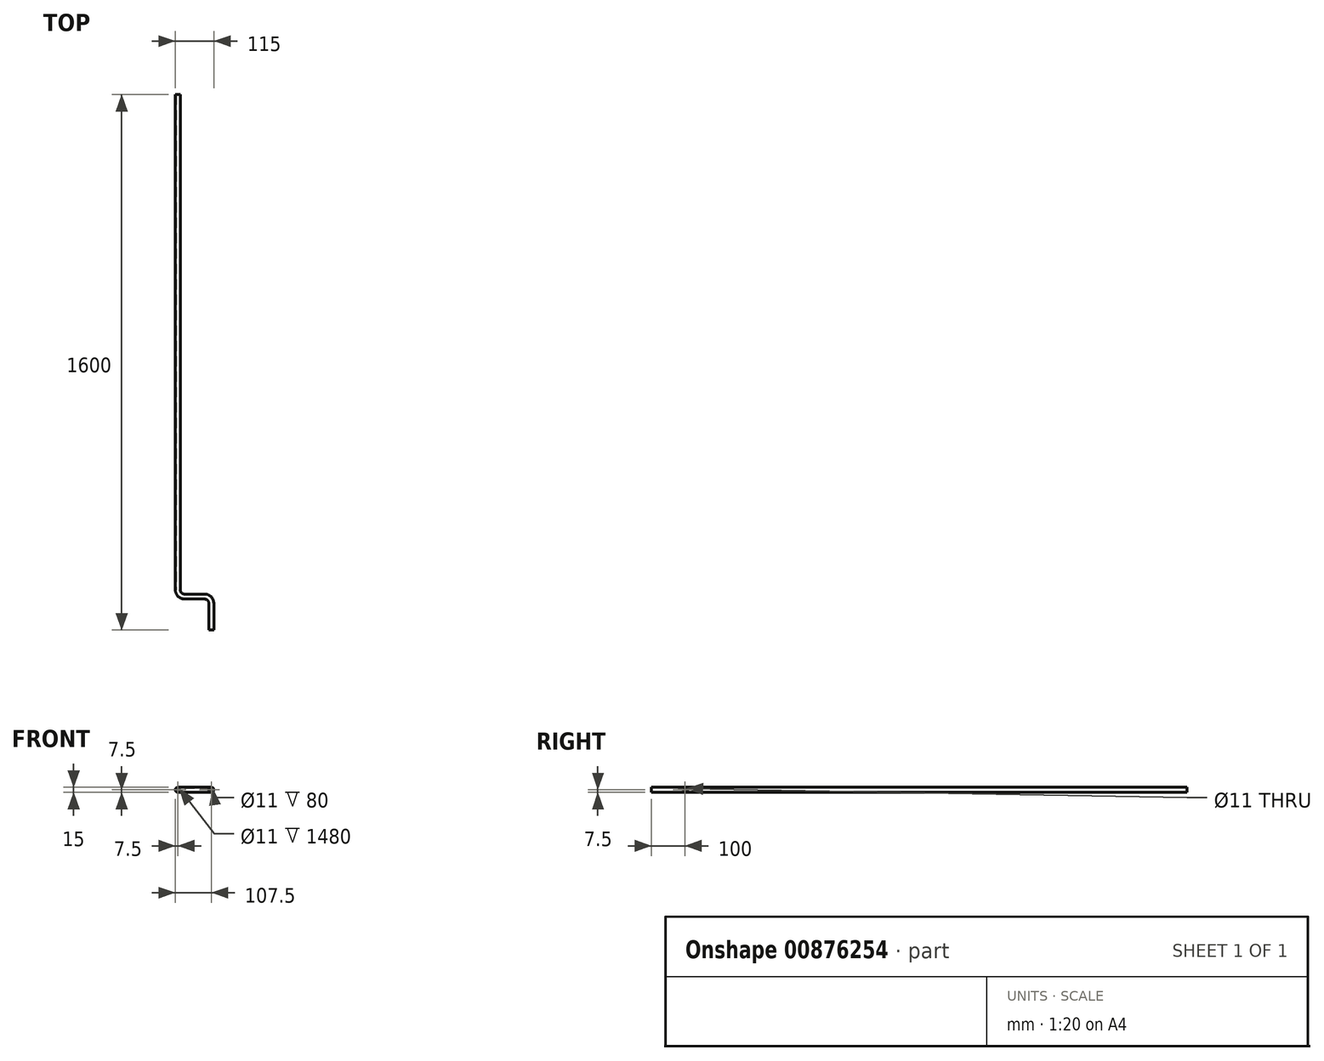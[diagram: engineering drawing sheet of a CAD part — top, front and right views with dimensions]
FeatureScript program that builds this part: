
annotation { "Feature Type Name" : "Feature", "Feature Type Description" : "" }
export const myFeature = defineFeature(function(context is Context, id is Id, definition is map)
    precondition{}
    {
        {
            var Q0;
            Q0=qCreatedBy(makeId("Front.planeOp"),FACE);
            var sketch = newSketch(context, id + "F0", { "sketchPlane" : qUnion([Q0])});
            skCircle(sketch, "E0", {"center": v(0, 0) * mm, "radius": 7.5 * mm});
            skCircle(sketch, "E1.0", {"center": v(0, 0) * mm, "radius": 5.5 * mm});
            skSolve(sketch);
        }
        {
            var Q0;
            Q0=qCreatedBy(makeId("Top.planeOp"),FACE);
            var sketch = newSketch(context, id + "F1", { "sketchPlane" : qUnion([Q0])});
            skLineSegment(sketch, "E2", {"start": v(0, 0) * mm, "end": v(0, -1480) * mm});
            skLineSegment(sketch, "E3", {"start": v(20, -1500) * mm, "end": v(80, -1500) * mm});
            skLineSegment(sketch, "E4", {"start": v(100, -1520) * mm, "end": v(100, -1600) * mm});
            skPoint(sketch, "E5.visualSharp", {"position": v(0, -1500) * mm});
            skArc(sketch, "E5.filletArc", {"start": v(0, -1480) * mm, "mid": v(5.86, -1494.14) * mm, "end": v(20, -1500) * mm});
            skPoint(sketch, "E6.visualSharp", {"position": v(100, -1500) * mm});
            skArc(sketch, "E6.filletArc", {"start": v(100, -1520) * mm, "mid": v(94.14, -1505.86) * mm, "end": v(80, -1500) * mm});
            skSolve(sketch);
        }
        {
            var Q0;
            Q0=makeQuery(id+"F0.imprint","IMPRINT",FACE,{"disambiguationData":[TD([[makeQuery(id+"F0.imprint","IMPRINT",EDGE,{"derivedFrom":sQuery(id+"F0.wireOp",EDGE,"E0")}),1.0]])]});
            var Q1;
            Q1=sQuery(id+"F1.wireOp",EDGE,"E2");
            var Q2;
            Q2=sQuery(id+"F1.wireOp",EDGE,"E5.filletArc");
            var Q3;
            Q3=sQuery(id+"F1.wireOp",EDGE,"E3");
            var Q4;
            Q4=sQuery(id+"F1.wireOp",EDGE,"E6.filletArc");
            var Q5;
            Q5=sQuery(id+"F1.wireOp",EDGE,"E4");
            sweep(context, id + "F2", {"profiles" : qUnion([Q0]), "path" : qUnion([Q1, Q2, Q3, Q4, Q5])});
        }
    });
